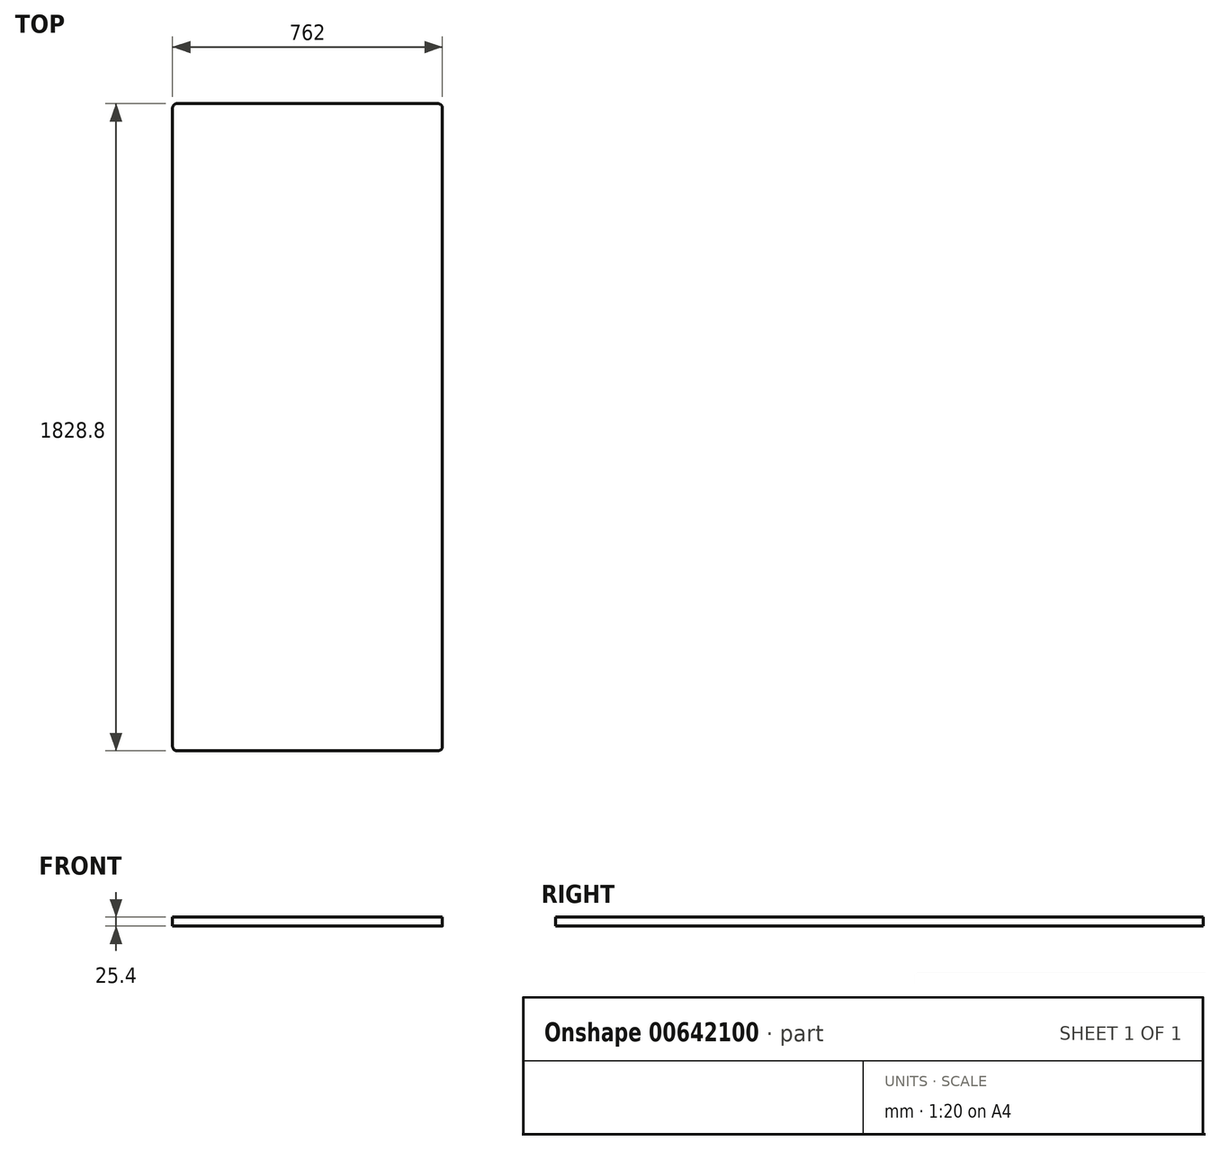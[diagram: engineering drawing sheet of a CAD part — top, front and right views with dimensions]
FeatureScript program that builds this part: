
annotation { "Feature Type Name" : "Feature", "Feature Type Description" : "" }
export const myFeature = defineFeature(function(context is Context, id is Id, definition is map)
    precondition{}
    {
        {
            var Q0;
            Q0=qCreatedBy(makeId("Top.planeOp"),FACE);
            var sketch = newSketch(context, id + "F0", { "sketchPlane" : qUnion([Q0])});
            skLineSegment(sketch, "E0.bottom", {"start": v(12.7, 0) * mm, "end": v(749.3, 0) * mm});
            skLineSegment(sketch, "E0.top", {"start": v(12.7, -1828.8) * mm, "end": v(749.3, -1828.8) * mm});
            skLineSegment(sketch, "E0.left", {"start": v(0, -12.7) * mm, "end": v(0, -1816.1) * mm});
            skLineSegment(sketch, "E0.right", {"start": v(762, -12.7) * mm, "end": v(762, -1816.1) * mm});
            skPoint(sketch, "E1.visualSharp", {"position": v(0, 0) * mm});
            skArc(sketch, "E1.filletArc", {"start": v(12.7, 0) * mm, "mid": v(3.72, -3.72) * mm, "end": v(0, -12.7) * mm});
            skPoint(sketch, "E2.visualSharp", {"position": v(762, 0) * mm});
            skArc(sketch, "E2.filletArc", {"start": v(762, -12.7) * mm, "mid": v(758.28, -3.72) * mm, "end": v(749.3, 0) * mm});
            skPoint(sketch, "E3.visualSharp", {"position": v(762, -1828.8) * mm});
            skArc(sketch, "E3.filletArc", {"start": v(749.3, -1828.8) * mm, "mid": v(758.28, -1825.08) * mm, "end": v(762, -1816.1) * mm});
            skPoint(sketch, "E4.visualSharp", {"position": v(0, -1828.8) * mm});
            skArc(sketch, "E4.filletArc", {"start": v(0, -1816.1) * mm, "mid": v(3.72, -1825.08) * mm, "end": v(12.7, -1828.8) * mm});
            skSolve(sketch);
        }
        {
            var Q0;
            Q0=makeQuery(id+"F0.imprint","IMPRINT",FACE,{"disambiguationData":[TD([[makeQuery(id+"F0.imprint","IMPRINT",EDGE,{"derivedFrom":sQuery(id+"F0.wireOp",EDGE,"E0.bottom")}),-1.0]])]});
            extrude(context, id + "F1", {"entities" : qUnion([Q0]), "depth" : 25.4 * mm, "offsetDistance" : 25.4 * mm});
        }
        {
            var Q0;
            Q0=makeQuery(id+"F1.opExtrude","CAP_FACE",FACE,{"disambiguationData":[OSD([sQuery(id+"F0.wireOp",EDGE,"E0.bottom"),sQuery(id+"F0.wireOp",EDGE,"E0.top"),sQuery(id+"F0.wireOp",EDGE,"E0.left"),sQuery(id+"F0.wireOp",EDGE,"E0.right"),sQuery(id+"F0.wireOp",EDGE,"E1.filletArc"),sQuery(id+"F0.wireOp",EDGE,"E2.filletArc"),sQuery(id+"F0.wireOp",EDGE,"E3.filletArc"),sQuery(id+"F0.wireOp",EDGE,"E4.filletArc")])],"isStart":false});
            var sketch = newSketch(context, id + "F2", { "sketchPlane" : qUnion([Q0])});
            skSolve(sketch);
        }
        {
            var Q0;
            Q0=makeQuery(id+"F1.opExtrude","SWEPT_FACE",FACE,{"disambiguationData":[OSD([sQuery(id+"F0.wireOp",EDGE,"E0.left")])]});
            var sketch = newSketch(context, id + "F3", { "sketchPlane" : qUnion([Q0])});
            skLineSegment(sketch, "E5.bottom", {"start": v(12.7, 25.4) * mm, "end": v(1816.1, 25.4) * mm});
            skLineSegment(sketch, "E5.top", {"start": v(12.7, 0) * mm, "end": v(1816.1, 0) * mm});
            skLineSegment(sketch, "E5.left", {"start": v(12.7, 25.4) * mm, "end": v(12.7, 0) * mm});
            skLineSegment(sketch, "E5.right", {"start": v(1816.1, 25.4) * mm, "end": v(1816.1, 0) * mm});
            skSolve(sketch);
        }
        {
            var Q0;
            Q0=makeQuery(id+"F3.imprint","IMPRINT",FACE,{"disambiguationData":[TD([[makeQuery(id+"F3.imprint","IMPRINT",EDGE,{"derivedFrom":sQuery(id+"F3.wireOp",EDGE,"E5.bottom")}),-1.0]])]});
            extrude(context, id + "F4", {"entities" : qUnion([Q0]), "operationType" : NewBodyOperationType.ADD, "depth" : 3.17 * mm, "offsetDistance" : 25.4 * mm});
        }
        {
            var Q0;
            Q0=makeQuery(id+"F4.opExtrude","CAP_FACE",FACE,{"disambiguationData":[OSD([sQuery(id+"F3.wireOp",EDGE,"E5.bottom"),sQuery(id+"F3.wireOp",EDGE,"E5.top"),sQuery(id+"F3.wireOp",EDGE,"E5.left"),sQuery(id+"F3.wireOp",EDGE,"E5.right")])],"isStart":false});
            extrude(context, id + "F5", {"entities" : qUnion([Q0]), "operationType" : NewBodyOperationType.REMOVE, "oppositeDirection" : true, "depth" : 3.17 * mm, "offsetDistance" : 25.4 * mm});
        }
    });
